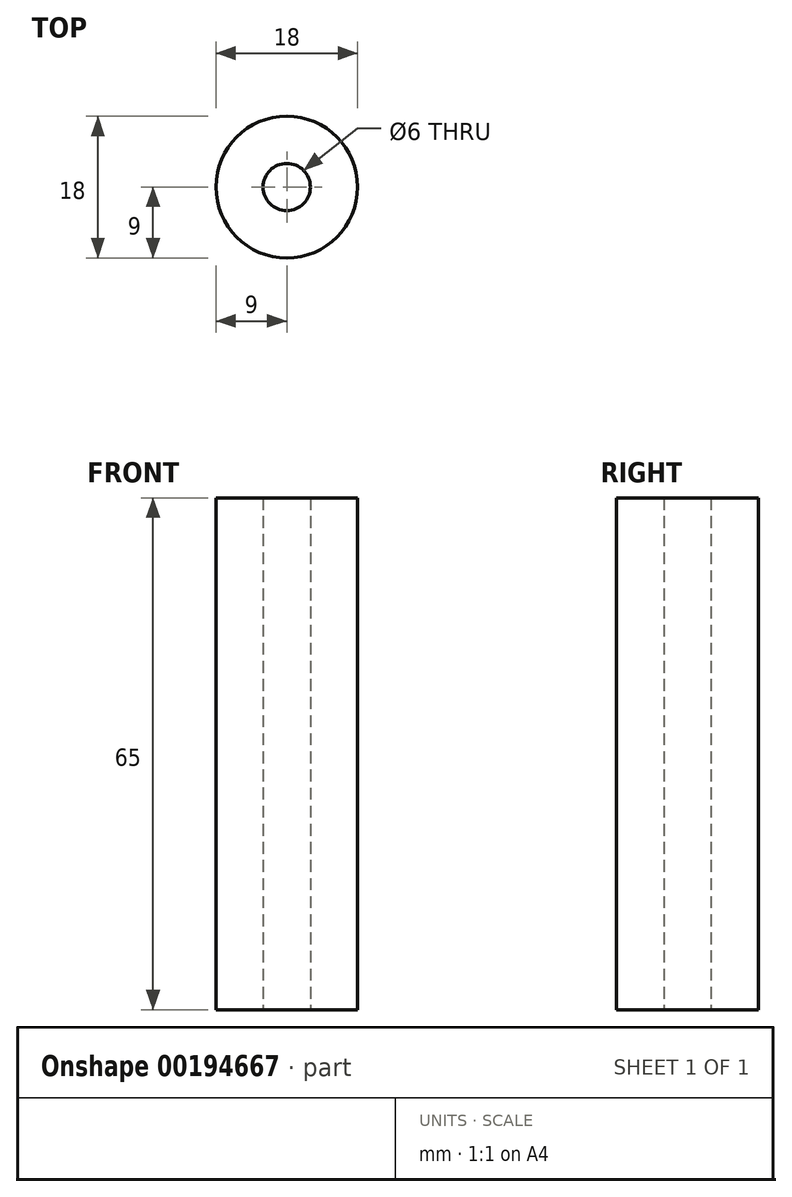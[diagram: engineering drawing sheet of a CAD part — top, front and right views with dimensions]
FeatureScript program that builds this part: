
annotation { "Feature Type Name" : "Feature", "Feature Type Description" : "" }
export const myFeature = defineFeature(function(context is Context, id is Id, definition is map)
    precondition{}
    {
        {
            var Q0;
            Q0=qCreatedBy(makeId("Top.planeOp"),FACE);
            var sketch = newSketch(context, id + "F0", { "sketchPlane" : qUnion([Q0])});
            skCircle(sketch, "E0", {"center": v(0, 0) * mm, "radius": 9 * mm});
            skCircle(sketch, "E1", {"center": v(0, 0) * mm, "radius": 3 * mm});
            skSolve(sketch);
        }
        {
            var Q0;
            Q0=makeQuery(id+"F0.imprint","IMPRINT",FACE,{"disambiguationData":[TD([[makeQuery(id+"F0.imprint","IMPRINT",EDGE,{"derivedFrom":sQuery(id+"F0.wireOp",EDGE,"E0")}),1.0]])]});
            extrude(context, id + "F1", {"entities" : qUnion([Q0]), "depth" : 65 * mm});
        }
    });
